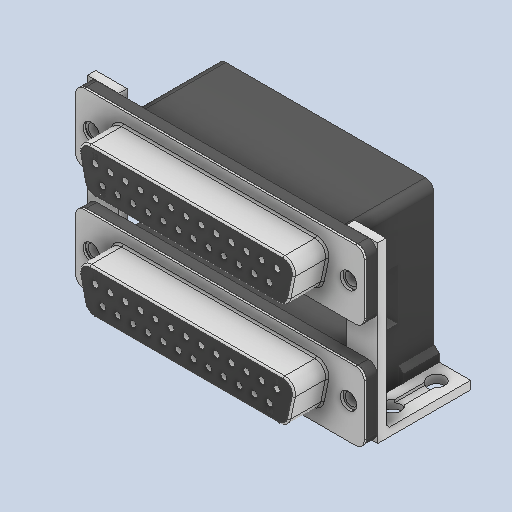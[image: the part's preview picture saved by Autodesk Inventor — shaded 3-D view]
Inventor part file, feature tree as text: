
AUTODESK INVENTOR PART (.ipt)
format: ipt  version: 2025 (Build 290162000, 162)  size: 871,424 bytes
history: native  units: in
note: dims shown in document units (in); Inventor stores cm internally (conversion verified against a paired STEP export)
features: extrude x1
ambient origin geometry x8: Origin, YZ Plane, XZ Plane, XY Plane, X Axis, Y Axis, Z Axis, Center Point
bodies: Solid1 (feature_tree)
feature tree (1):
  extrude  "Extrude32"  [1 undecoded]
note: 1 required parameter value undecoded (feature->parameter linkage not recoverable at this tier; creation-order binding heuristic only, values carry confidence <= 0.55)
